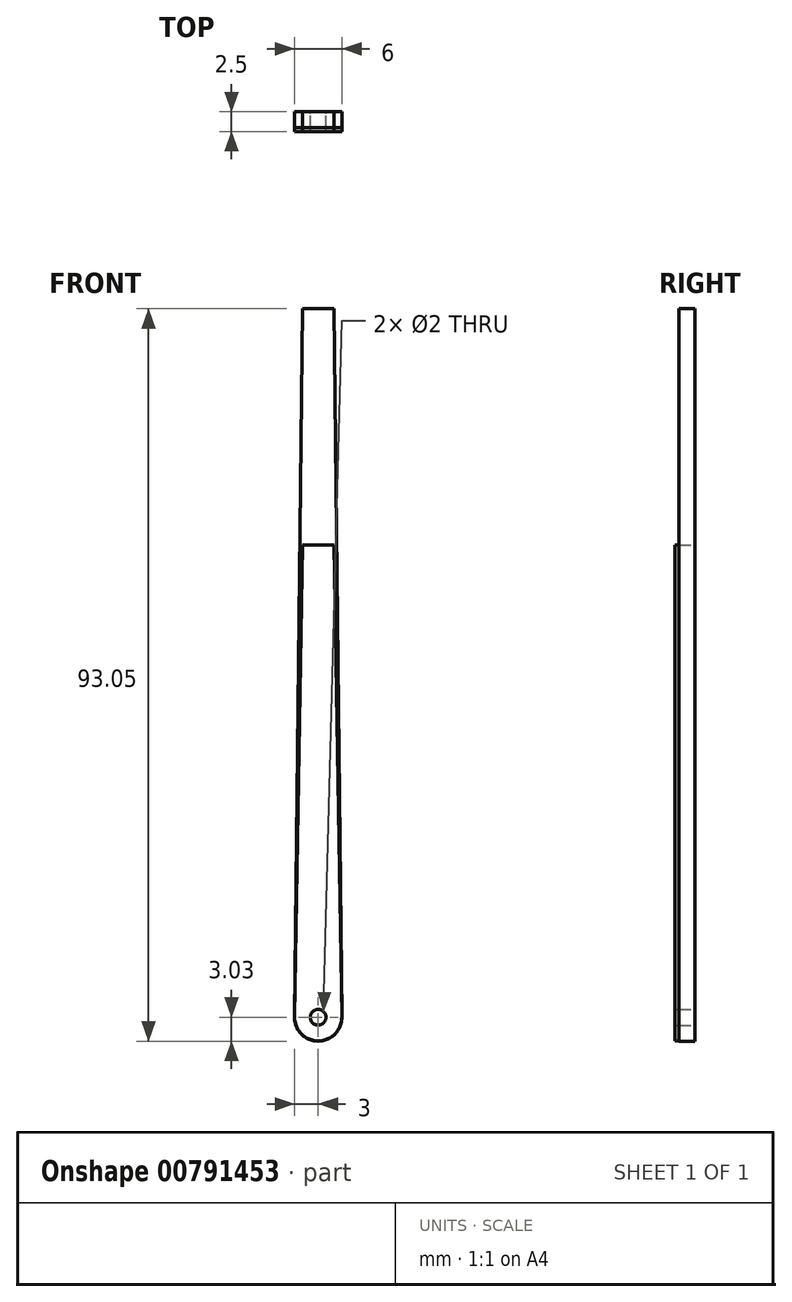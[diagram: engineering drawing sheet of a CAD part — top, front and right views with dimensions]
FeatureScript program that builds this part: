
annotation { "Feature Type Name" : "Feature", "Feature Type Description" : "" }
export const myFeature = defineFeature(function(context is Context, id is Id, definition is map)
    precondition{}
    {
        {
            var Q0;
            Q0=qCreatedBy(makeId("Front.planeOp"),FACE);
            var sketch = newSketch(context, id + "F0", { "sketchPlane" : qUnion([Q0])});
            skLineSegment(sketch, "E0", {"start": v(0, 0) * mm, "end": v(0, 90) * mm, "construction": true});
            skLineSegment(sketch, "E1", {"start": v(-3, 0) * mm, "end": v(-2, 90.02) * mm});
            skLineSegment(sketch, "E2.MirrorCS", {"start": v(3, 0) * mm, "end": v(2, 90.02) * mm});
            skArc(sketch, "E3", {"start": v(-3, 0) * mm, "mid": v(0, -3.03) * mm, "end": v(3, 0) * mm});
            skCircle(sketch, "E4", {"center": v(0, 0) * mm, "radius": 1 * mm});
            skLineSegment(sketch, "E5", {"start": v(-2, 90.02) * mm, "end": v(2, 90.02) * mm});
            skSolve(sketch);
        }
        {
            var Q0;
            Q0 = qSketchRegion(id + "F0", true);
            extrude(context, id + "F1", {"entities" : qUnion([Q0]), "depth" : 2 * mm, "offsetDistance" : 25 * mm});
        }
        {
            var Q0;
            Q0=qCreatedBy(makeId("Front.planeOp"),FACE);
            var sketch = newSketch(context, id + "F2", { "sketchPlane" : qUnion([Q0])});
            skLineSegment(sketch, "E6", {"start": v(0, 0) * mm, "end": v(0, 60) * mm, "construction": true});
            skLineSegment(sketch, "E7", {"start": v(-3, 0.05) * mm, "end": v(-2, 60) * mm});
            skLineSegment(sketch, "E8.MirrorCS", {"start": v(3, 0.05) * mm, "end": v(2, 60) * mm});
            skArc(sketch, "E9", {"start": v(-3, 0.05) * mm, "mid": v(0, -3) * mm, "end": v(3, 0.05) * mm});
            skCircle(sketch, "E10", {"center": v(0, 0) * mm, "radius": 1 * mm});
            skLineSegment(sketch, "E11", {"start": v(-2, 60) * mm, "end": v(2, 60) * mm});
            skSolve(sketch);
        }
        {
            var Q0;
            Q0 = qSketchRegion(id + "F2", true);
            extrude(context, id + "F3", {"entities" : qUnion([Q0]), "depth" : 2.5 * mm, "offsetDistance" : 25 * mm});
        }
    });
